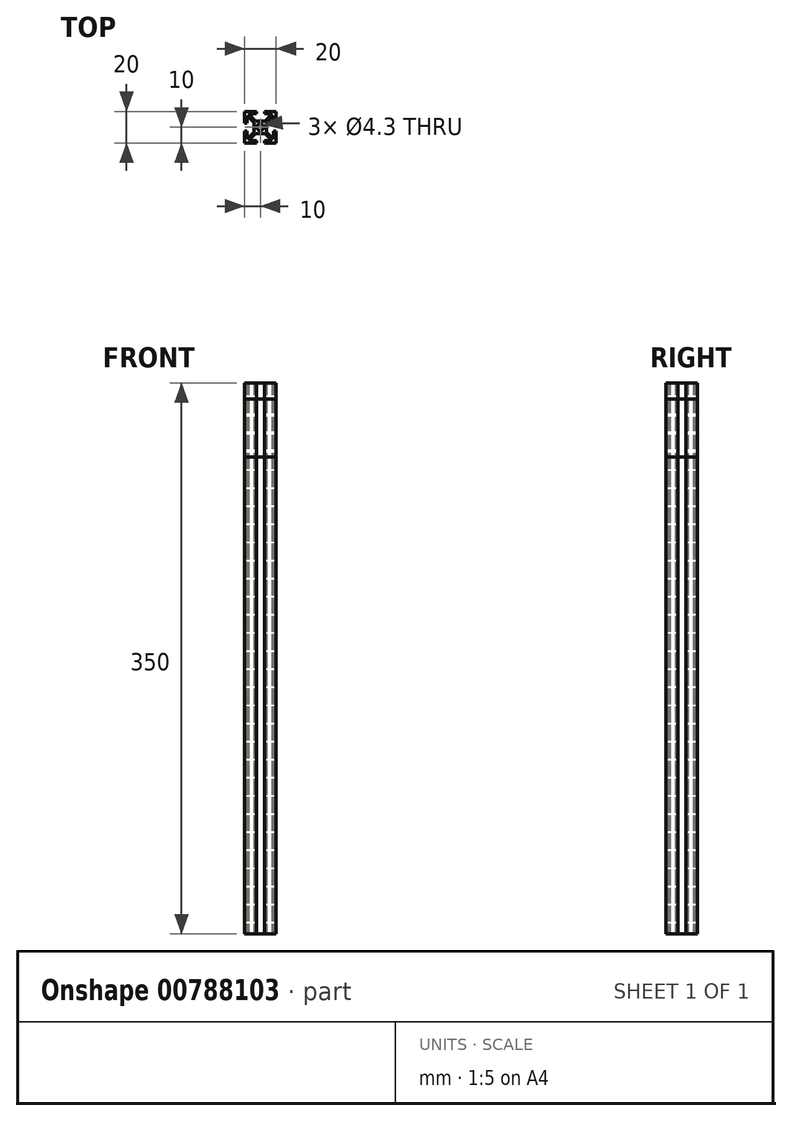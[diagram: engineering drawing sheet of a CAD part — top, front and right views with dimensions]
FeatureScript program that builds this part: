
annotation { "Feature Type Name" : "Feature", "Feature Type Description" : "" }
export const myFeature = defineFeature(function(context is Context, id is Id, definition is map)
    precondition{}
    {
        {
            var Q0;
            Q0=qCreatedBy(makeId("Top.planeOp"),FACE);
            var sketch = newSketch(context, id + "F0", { "sketchPlane" : qUnion([Q0])});
            skCircle(sketch, "E0", {"center": v(0, 0) * mm, "radius": 2.15 * mm});
            skLineSegment(sketch, "E1.bottom", {"start": v(10, 10) * mm, "end": v(-10, 10) * mm});
            skLineSegment(sketch, "E1.top", {"start": v(10, -10) * mm, "end": v(-10, -10) * mm});
            skLineSegment(sketch, "E1.left", {"start": v(10, 10) * mm, "end": v(10, -10) * mm});
            skLineSegment(sketch, "E1.right", {"start": v(-10, 10) * mm, "end": v(-10, -10) * mm});
            skLineSegment(sketch, "E2.bottom", {"start": v(8.5, 8.5) * mm, "end": v(-8.5, 8.5) * mm});
            skLineSegment(sketch, "E2.top", {"start": v(8.5, -8.5) * mm, "end": v(-8.5, -8.5) * mm});
            skLineSegment(sketch, "E2.left", {"start": v(8.5, 8.5) * mm, "end": v(8.5, -8.5) * mm});
            skLineSegment(sketch, "E2.right", {"start": v(-8.5, 8.5) * mm, "end": v(-8.5, -8.5) * mm});
            skLineSegment(sketch, "E3.bottom", {"start": v(4, 4) * mm, "end": v(-4, 4) * mm});
            skLineSegment(sketch, "E3.top", {"start": v(4, -4) * mm, "end": v(-4, -4) * mm});
            skLineSegment(sketch, "E3.left", {"start": v(4, 4) * mm, "end": v(4, -4) * mm});
            skLineSegment(sketch, "E3.right", {"start": v(-4, 4) * mm, "end": v(-4, -4) * mm});
            skLineSegment(sketch, "E4", {"start": v(8.5, 8.5) * mm, "end": v(-8.5, -8.5) * mm, "construction": true});
            skLineSegment(sketch, "E5", {"start": v(-8.5, 8.5) * mm, "end": v(8.5, -8.5) * mm, "construction": true});
            skLineSegment(sketch, "E6.0", {"start": v(-9.03, 7.97) * mm, "end": v(7.97, -9.03) * mm});
            skLineSegment(sketch, "E7.0", {"start": v(-7.97, 9.03) * mm, "end": v(9.03, -7.97) * mm});
            skLineSegment(sketch, "E8.0", {"start": v(7.97, 9.03) * mm, "end": v(-9.03, -7.97) * mm});
            skLineSegment(sketch, "E9.0", {"start": v(9.03, 7.97) * mm, "end": v(-7.97, -9.03) * mm});
            skLineSegment(sketch, "E10", {"start": v(0, 10) * mm, "end": v(0, -10) * mm, "construction": true});
            skLineSegment(sketch, "E11", {"start": v(-10, 0) * mm, "end": v(10, 0) * mm, "construction": true});
            skLineSegment(sketch, "E12.0", {"start": v(-10, -2.5) * mm, "end": v(10, -2.5) * mm});
            skLineSegment(sketch, "E13.0", {"start": v(-10, 2.5) * mm, "end": v(10, 2.5) * mm});
            skLineSegment(sketch, "E14.0", {"start": v(-2.5, 10) * mm, "end": v(-2.5, -10) * mm});
            skLineSegment(sketch, "E15.0", {"start": v(2.5, 10) * mm, "end": v(2.5, -10) * mm});
            skSolve(sketch);
        }
        {
            var Q0;
            {var subQ7=sQuery(id+"F0.wireOp",EDGE,"E1.right");var subQ8=sQuery(id+"F0.wireOp",EDGE,"E1.bottom");var subQ9=makeQuery(id+"F0.imprint","INTERSECT",VERTEX,{"derivedFrom":[subQ8,subQ7]});Q0=makeQuery(id+"F0.imprint","IMPRINT",FACE,{"disambiguationData":[TD([[makeQuery(id+"F0.imprint","IMPRINT",EDGE,{"disambiguationData":[TD([[subQ9,1.0]])],"derivedFrom":subQ8}),1.0]])]});}
            var Q1;
            {var subQ7=sQuery(id+"F0.wireOp",EDGE,"E2.right");var subQ8=sQuery(id+"F0.wireOp",EDGE,"E2.bottom");var subQ9=makeQuery(id+"F0.imprint","INTERSECT",VERTEX,{"derivedFrom":[subQ8,subQ7]});Q1=makeQuery(id+"F0.imprint","IMPRINT",FACE,{"disambiguationData":[TD([[makeQuery(id+"F0.imprint","IMPRINT",EDGE,{"disambiguationData":[TD([[subQ9,1.0]])],"derivedFrom":subQ8}),1.0]])]});}
            var Q2;
            {var subQ1=sQuery(id+"F0.wireOp",EDGE,"E3.right");var subQ5=sQuery(id+"F0.wireOp",EDGE,"E13.0");var subQ10=makeQuery(id+"F0.imprint","INTERSECT",VERTEX,{"derivedFrom":[subQ1,subQ5]});Q2=makeQuery(id+"F0.imprint","IMPRINT",FACE,{"disambiguationData":[TD([[makeQuery(id+"F0.imprint","IMPRINT",EDGE,{"disambiguationData":[TD([[subQ10,-1.0]])],"derivedFrom":subQ1}),1.0]])]});}
            var Q3;
            {var subQ1=sQuery(id+"F0.wireOp",EDGE,"E3.bottom");var subQ6=sQuery(id+"F0.wireOp",EDGE,"E3.right");var subQ10=makeQuery(id+"F0.imprint","INTERSECT",VERTEX,{"derivedFrom":[subQ1,subQ6]});Q3=makeQuery(id+"F0.imprint","IMPRINT",FACE,{"disambiguationData":[TD([[makeQuery(id+"F0.imprint","IMPRINT",EDGE,{"disambiguationData":[TD([[subQ10,1.0]])],"derivedFrom":subQ1}),1.0]])]});}
            var Q4;
            {var subQ0=sQuery(id+"F0.wireOp",EDGE,"E6.0");var subQ1=sQuery(id+"F0.wireOp",EDGE,"E3.right");var subQ2=makeQuery(id+"F0.imprint","INTERSECT",VERTEX,{"derivedFrom":[subQ1,subQ0]});Q4=makeQuery(id+"F0.imprint","IMPRINT",FACE,{"disambiguationData":[TD([[makeQuery(id+"F0.imprint","IMPRINT",EDGE,{"disambiguationData":[TD([[subQ2,-1.0]])],"derivedFrom":subQ1}),1.0]])]});}
            var Q5;
            {var subQ0=sQuery(id+"F0.wireOp",EDGE,"E12.0");var subQ1=sQuery(id+"F0.wireOp",EDGE,"E3.right");var subQ2=makeQuery(id+"F0.imprint","INTERSECT",VERTEX,{"derivedFrom":[subQ1,subQ0]});Q5=makeQuery(id+"F0.imprint","IMPRINT",FACE,{"disambiguationData":[TD([[makeQuery(id+"F0.imprint","IMPRINT",EDGE,{"disambiguationData":[TD([[subQ2,-1.0]])],"derivedFrom":subQ1}),1.0]])]});}
            var Q6;
            {var subQ1=sQuery(id+"F0.wireOp",EDGE,"E3.top");var subQ6=sQuery(id+"F0.wireOp",EDGE,"E3.right");var subQ10=makeQuery(id+"F0.imprint","INTERSECT",VERTEX,{"derivedFrom":[subQ1,subQ6]});Q6=makeQuery(id+"F0.imprint","IMPRINT",FACE,{"disambiguationData":[TD([[makeQuery(id+"F0.imprint","IMPRINT",EDGE,{"disambiguationData":[TD([[subQ10,1.0]])],"derivedFrom":subQ1}),-1.0]])]});}
            var Q7;
            {var subQ5=sQuery(id+"F0.wireOp",EDGE,"E2.right");var subQ8=sQuery(id+"F0.wireOp",EDGE,"E2.top");var subQ11=makeQuery(id+"F0.imprint","INTERSECT",VERTEX,{"derivedFrom":[subQ8,subQ5]});Q7=makeQuery(id+"F0.imprint","IMPRINT",FACE,{"disambiguationData":[TD([[makeQuery(id+"F0.imprint","IMPRINT",EDGE,{"disambiguationData":[TD([[subQ11,1.0]])],"derivedFrom":subQ8}),-1.0]])]});}
            var Q8;
            {var subQ0=sQuery(id+"F0.wireOp",EDGE,"E14.0");var subQ1=sQuery(id+"F0.wireOp",EDGE,"E8.0");var subQ2=makeQuery(id+"F0.imprint","INTERSECT",VERTEX,{"derivedFrom":[subQ1,subQ0]});Q8=makeQuery(id+"F0.imprint","IMPRINT",FACE,{"disambiguationData":[TD([[makeQuery(id+"F0.imprint","IMPRINT",EDGE,{"disambiguationData":[TD([[subQ2,-1.0]])],"derivedFrom":subQ1}),1.0]])]});}
            var Q9;
            {var subQ0=sQuery(id+"F0.wireOp",EDGE,"E13.0");var subQ1=sQuery(id+"F0.wireOp",EDGE,"E6.0");var subQ2=makeQuery(id+"F0.imprint","INTERSECT",VERTEX,{"derivedFrom":[subQ1,subQ0]});Q9=makeQuery(id+"F0.imprint","IMPRINT",FACE,{"disambiguationData":[TD([[makeQuery(id+"F0.imprint","IMPRINT",EDGE,{"disambiguationData":[TD([[subQ2,-1.0]])],"derivedFrom":subQ1}),1.0]])]});}
            var Q10;
            {var subQ0=sQuery(id+"F0.wireOp",EDGE,"E14.0");var subQ1=sQuery(id+"F0.wireOp",EDGE,"E3.bottom");var subQ2=makeQuery(id+"F0.imprint","INTERSECT",VERTEX,{"derivedFrom":[subQ1,subQ0]});Q10=makeQuery(id+"F0.imprint","IMPRINT",FACE,{"disambiguationData":[TD([[makeQuery(id+"F0.imprint","IMPRINT",EDGE,{"disambiguationData":[TD([[subQ2,-1.0]])],"derivedFrom":subQ1}),1.0]])]});}
            var Q11;
            {var subQ5=sQuery(id+"F0.wireOp",EDGE,"E15.0");var subQ9=sQuery(id+"F0.wireOp",EDGE,"E3.bottom");var subQ11=makeQuery(id+"F0.imprint","INTERSECT",VERTEX,{"derivedFrom":[subQ9,subQ5]});Q11=makeQuery(id+"F0.imprint","IMPRINT",FACE,{"disambiguationData":[TD([[makeQuery(id+"F0.imprint","IMPRINT",EDGE,{"disambiguationData":[TD([[subQ11,-1.0]])],"derivedFrom":subQ9}),1.0]])]});}
            var Q12;
            {var subQ0=sQuery(id+"F0.wireOp",EDGE,"E14.0");var subQ1=sQuery(id+"F0.wireOp",EDGE,"E7.0");var subQ2=makeQuery(id+"F0.imprint","INTERSECT",VERTEX,{"derivedFrom":[subQ1,subQ0]});Q12=makeQuery(id+"F0.imprint","IMPRINT",FACE,{"disambiguationData":[TD([[makeQuery(id+"F0.imprint","IMPRINT",EDGE,{"disambiguationData":[TD([[subQ2,-1.0]])],"derivedFrom":subQ1}),-1.0]])]});}
            var Q13;
            {var subQ0=sQuery(id+"F0.wireOp",EDGE,"E15.0");var subQ1=sQuery(id+"F0.wireOp",EDGE,"E8.0");var subQ2=makeQuery(id+"F0.imprint","INTERSECT",VERTEX,{"derivedFrom":[subQ1,subQ0]});Q13=makeQuery(id+"F0.imprint","IMPRINT",FACE,{"disambiguationData":[TD([[makeQuery(id+"F0.imprint","IMPRINT",EDGE,{"disambiguationData":[TD([[subQ2,-1.0]])],"derivedFrom":subQ1}),1.0]])]});}
            var Q14;
            {var subQ1=sQuery(id+"F0.wireOp",EDGE,"E3.left");var subQ6=sQuery(id+"F0.wireOp",EDGE,"E3.bottom");var subQ10=makeQuery(id+"F0.imprint","INTERSECT",VERTEX,{"derivedFrom":[subQ6,subQ1]});Q14=makeQuery(id+"F0.imprint","IMPRINT",FACE,{"disambiguationData":[TD([[makeQuery(id+"F0.imprint","IMPRINT",EDGE,{"disambiguationData":[TD([[subQ10,-1.0]])],"derivedFrom":subQ6}),1.0]])]});}
            var Q15;
            {var subQ0=sQuery(id+"F0.wireOp",EDGE,"E8.0");var subQ1=sQuery(id+"F0.wireOp",EDGE,"E3.bottom");var subQ2=makeQuery(id+"F0.imprint","INTERSECT",VERTEX,{"derivedFrom":[subQ1,subQ0]});Q15=makeQuery(id+"F0.imprint","IMPRINT",FACE,{"disambiguationData":[TD([[makeQuery(id+"F0.imprint","IMPRINT",EDGE,{"disambiguationData":[TD([[subQ2,-1.0]])],"derivedFrom":subQ1}),1.0]])]});}
            var Q16;
            {var subQ0=sQuery(id+"F0.wireOp",EDGE,"E9.0");var subQ1=sQuery(id+"F0.wireOp",EDGE,"E3.left");var subQ2=makeQuery(id+"F0.imprint","INTERSECT",VERTEX,{"derivedFrom":[subQ1,subQ0]});Q16=makeQuery(id+"F0.imprint","IMPRINT",FACE,{"disambiguationData":[TD([[makeQuery(id+"F0.imprint","IMPRINT",EDGE,{"disambiguationData":[TD([[subQ2,-1.0]])],"derivedFrom":subQ1}),-1.0]])]});}
            var Q17;
            {var subQ0=sQuery(id+"F0.wireOp",EDGE,"E13.0");var subQ9=sQuery(id+"F0.wireOp",EDGE,"E3.left");var subQ11=makeQuery(id+"F0.imprint","INTERSECT",VERTEX,{"derivedFrom":[subQ9,subQ0]});Q17=makeQuery(id+"F0.imprint","IMPRINT",FACE,{"disambiguationData":[TD([[makeQuery(id+"F0.imprint","IMPRINT",EDGE,{"disambiguationData":[TD([[subQ11,-1.0]])],"derivedFrom":subQ9}),-1.0]])]});}
            var Q18;
            {var subQ1=sQuery(id+"F0.wireOp",EDGE,"E3.top");var subQ6=sQuery(id+"F0.wireOp",EDGE,"E3.left");var subQ10=makeQuery(id+"F0.imprint","INTERSECT",VERTEX,{"derivedFrom":[subQ1,subQ6]});Q18=makeQuery(id+"F0.imprint","IMPRINT",FACE,{"disambiguationData":[TD([[makeQuery(id+"F0.imprint","IMPRINT",EDGE,{"disambiguationData":[TD([[subQ10,-1.0]])],"derivedFrom":subQ1}),-1.0]])]});}
            var Q19;
            {var subQ0=sQuery(id+"F0.wireOp",EDGE,"E15.0");var subQ1=sQuery(id+"F0.wireOp",EDGE,"E7.0");var subQ2=makeQuery(id+"F0.imprint","INTERSECT",VERTEX,{"derivedFrom":[subQ1,subQ0]});Q19=makeQuery(id+"F0.imprint","IMPRINT",FACE,{"disambiguationData":[TD([[makeQuery(id+"F0.imprint","IMPRINT",EDGE,{"disambiguationData":[TD([[subQ2,-1.0]])],"derivedFrom":subQ1}),-1.0]])]});}
            var Q20;
            {var subQ0=sQuery(id+"F0.wireOp",EDGE,"E12.0");var subQ1=sQuery(id+"F0.wireOp",EDGE,"E6.0");var subQ2=makeQuery(id+"F0.imprint","INTERSECT",VERTEX,{"derivedFrom":[subQ1,subQ0]});Q20=makeQuery(id+"F0.imprint","IMPRINT",FACE,{"disambiguationData":[TD([[makeQuery(id+"F0.imprint","IMPRINT",EDGE,{"disambiguationData":[TD([[subQ2,-1.0]])],"derivedFrom":subQ1}),1.0]])]});}
            var Q21;
            {var subQ7=sQuery(id+"F0.wireOp",EDGE,"E15.0");var subQ9=sQuery(id+"F0.wireOp",EDGE,"E3.top");var subQ11=makeQuery(id+"F0.imprint","INTERSECT",VERTEX,{"derivedFrom":[subQ9,subQ7]});Q21=makeQuery(id+"F0.imprint","IMPRINT",FACE,{"disambiguationData":[TD([[makeQuery(id+"F0.imprint","IMPRINT",EDGE,{"disambiguationData":[TD([[subQ11,-1.0]])],"derivedFrom":subQ9}),-1.0]])]});}
            var Q22;
            {var subQ0=sQuery(id+"F0.wireOp",EDGE,"E14.0");var subQ1=sQuery(id+"F0.wireOp",EDGE,"E3.top");var subQ2=makeQuery(id+"F0.imprint","INTERSECT",VERTEX,{"derivedFrom":[subQ1,subQ0]});Q22=makeQuery(id+"F0.imprint","IMPRINT",FACE,{"disambiguationData":[TD([[makeQuery(id+"F0.imprint","IMPRINT",EDGE,{"disambiguationData":[TD([[subQ2,-1.0]])],"derivedFrom":subQ1}),-1.0]])]});}
            var Q23;
            {var subQ0=sQuery(id+"F0.wireOp",EDGE,"E12.0");var subQ1=sQuery(id+"F0.wireOp",EDGE,"E3.left");var subQ2=makeQuery(id+"F0.imprint","INTERSECT",VERTEX,{"derivedFrom":[subQ1,subQ0]});Q23=makeQuery(id+"F0.imprint","IMPRINT",FACE,{"disambiguationData":[TD([[makeQuery(id+"F0.imprint","IMPRINT",EDGE,{"disambiguationData":[TD([[subQ2,-1.0]])],"derivedFrom":subQ1}),-1.0]])]});}
            var Q24;
            {var subQ0=sQuery(id+"F0.wireOp",EDGE,"E6.0");var subQ1=sQuery(id+"F0.wireOp",EDGE,"E3.top");var subQ2=makeQuery(id+"F0.imprint","INTERSECT",VERTEX,{"derivedFrom":[subQ1,subQ0]});Q24=makeQuery(id+"F0.imprint","IMPRINT",FACE,{"disambiguationData":[TD([[makeQuery(id+"F0.imprint","IMPRINT",EDGE,{"disambiguationData":[TD([[subQ2,-1.0]])],"derivedFrom":subQ1}),-1.0]])]});}
            var Q25;
            {var subQ5=sQuery(id+"F0.wireOp",EDGE,"E2.left");var subQ6=sQuery(id+"F0.wireOp",EDGE,"E2.top");var subQ7=makeQuery(id+"F0.imprint","INTERSECT",VERTEX,{"derivedFrom":[subQ6,subQ5]});Q25=makeQuery(id+"F0.imprint","IMPRINT",FACE,{"disambiguationData":[TD([[makeQuery(id+"F0.imprint","IMPRINT",EDGE,{"disambiguationData":[TD([[subQ7,-1.0]])],"derivedFrom":subQ6}),-1.0]])]});}
            var Q26;
            {var subQ0=sQuery(id+"F0.wireOp",EDGE,"E12.0");var subQ1=sQuery(id+"F0.wireOp",EDGE,"E9.0");var subQ2=makeQuery(id+"F0.imprint","INTERSECT",VERTEX,{"derivedFrom":[subQ1,subQ0]});Q26=makeQuery(id+"F0.imprint","IMPRINT",FACE,{"disambiguationData":[TD([[makeQuery(id+"F0.imprint","IMPRINT",EDGE,{"disambiguationData":[TD([[subQ2,-1.0]])],"derivedFrom":subQ1}),-1.0]])]});}
            var Q27;
            {var subQ0=sQuery(id+"F0.wireOp",EDGE,"E13.0");var subQ1=sQuery(id+"F0.wireOp",EDGE,"E9.0");var subQ2=makeQuery(id+"F0.imprint","INTERSECT",VERTEX,{"derivedFrom":[subQ1,subQ0]});Q27=makeQuery(id+"F0.imprint","IMPRINT",FACE,{"disambiguationData":[TD([[makeQuery(id+"F0.imprint","IMPRINT",EDGE,{"disambiguationData":[TD([[subQ2,-1.0]])],"derivedFrom":subQ1}),-1.0]])]});}
            var Q28;
            {var subQ7=sQuery(id+"F0.wireOp",EDGE,"E2.left");var subQ8=sQuery(id+"F0.wireOp",EDGE,"E2.bottom");var subQ9=makeQuery(id+"F0.imprint","INTERSECT",VERTEX,{"derivedFrom":[subQ8,subQ7]});Q28=makeQuery(id+"F0.imprint","IMPRINT",FACE,{"disambiguationData":[TD([[makeQuery(id+"F0.imprint","IMPRINT",EDGE,{"disambiguationData":[TD([[subQ9,-1.0]])],"derivedFrom":subQ8}),1.0]])]});}
            var Q29;
            {var subQ9=sQuery(id+"F0.wireOp",EDGE,"E1.left");var subQ10=sQuery(id+"F0.wireOp",EDGE,"E1.bottom");var subQ11=makeQuery(id+"F0.imprint","INTERSECT",VERTEX,{"derivedFrom":[subQ10,subQ9]});Q29=makeQuery(id+"F0.imprint","IMPRINT",FACE,{"disambiguationData":[TD([[makeQuery(id+"F0.imprint","IMPRINT",EDGE,{"disambiguationData":[TD([[subQ11,-1.0]])],"derivedFrom":subQ10}),1.0]])]});}
            var Q30;
            {var subQ7=sQuery(id+"F0.wireOp",EDGE,"E1.left");var subQ10=sQuery(id+"F0.wireOp",EDGE,"E1.top");var subQ12=makeQuery(id+"F0.imprint","INTERSECT",VERTEX,{"derivedFrom":[subQ10,subQ7]});Q30=makeQuery(id+"F0.imprint","IMPRINT",FACE,{"disambiguationData":[TD([[makeQuery(id+"F0.imprint","IMPRINT",EDGE,{"disambiguationData":[TD([[subQ12,-1.0]])],"derivedFrom":subQ10}),-1.0]])]});}
            var Q31;
            {var subQ4=sQuery(id+"F0.wireOp",EDGE,"E1.right");var subQ5=sQuery(id+"F0.wireOp",EDGE,"E1.top");var subQ6=makeQuery(id+"F0.imprint","INTERSECT",VERTEX,{"derivedFrom":[subQ5,subQ4]});Q31=makeQuery(id+"F0.imprint","IMPRINT",FACE,{"disambiguationData":[TD([[makeQuery(id+"F0.imprint","IMPRINT",EDGE,{"disambiguationData":[TD([[subQ6,1.0]])],"derivedFrom":subQ5}),-1.0]])]});}
            var Q32;
            {var subQ1=sQuery(id+"F0.wireOp",EDGE,"E7.0");var subQ7=sQuery(id+"F0.wireOp",EDGE,"E0");var subQ8=makeQuery(id+"F0.imprint","INTERSECT",VERTEX,{"disambiguationData":[OD(0.0)],"derivedFrom":[subQ7,subQ1]});Q32=makeQuery(id+"F0.imprint","IMPRINT",FACE,{"disambiguationData":[TD([[makeQuery(id+"F0.imprint","IMPRINT",EDGE,{"disambiguationData":[TD([[subQ8,-1.0]])],"derivedFrom":subQ7}),-1.0]])]});}
            var Q33;
            {var subQ0=sQuery(id+"F0.wireOp",EDGE,"E8.0");var subQ1=sQuery(id+"F0.wireOp",EDGE,"E0");var subQ2=makeQuery(id+"F0.imprint","INTERSECT",VERTEX,{"disambiguationData":[OD(0.0)],"derivedFrom":[subQ1,subQ0]});Q33=makeQuery(id+"F0.imprint","IMPRINT",FACE,{"disambiguationData":[TD([[makeQuery(id+"F0.imprint","IMPRINT",EDGE,{"disambiguationData":[TD([[subQ2,-1.0]])],"derivedFrom":subQ1}),-1.0]])]});}
            var Q34;
            {var subQ1=sQuery(id+"F0.wireOp",EDGE,"E8.0");var subQ5=sQuery(id+"F0.wireOp",EDGE,"E0");var subQ6=makeQuery(id+"F0.imprint","INTERSECT",VERTEX,{"disambiguationData":[OD(0.0)],"derivedFrom":[subQ5,subQ1]});Q34=makeQuery(id+"F0.imprint","IMPRINT",FACE,{"disambiguationData":[TD([[makeQuery(id+"F0.imprint","IMPRINT",EDGE,{"disambiguationData":[TD([[subQ6,1.0]])],"derivedFrom":subQ5}),-1.0]])]});}
            var Q35;
            {var subQ0=sQuery(id+"F0.wireOp",EDGE,"E9.0");var subQ1=sQuery(id+"F0.wireOp",EDGE,"E0");var subQ2=makeQuery(id+"F0.imprint","INTERSECT",VERTEX,{"disambiguationData":[OD(0.0)],"derivedFrom":[subQ1,subQ0]});Q35=makeQuery(id+"F0.imprint","IMPRINT",FACE,{"disambiguationData":[TD([[makeQuery(id+"F0.imprint","IMPRINT",EDGE,{"disambiguationData":[TD([[subQ2,1.0]])],"derivedFrom":subQ1}),-1.0]])]});}
            var Q36;
            {var subQ1=sQuery(id+"F0.wireOp",EDGE,"E6.0");var subQ7=sQuery(id+"F0.wireOp",EDGE,"E0");var subQ9=makeQuery(id+"F0.imprint","INTERSECT",VERTEX,{"disambiguationData":[OD(1.0)],"derivedFrom":[subQ7,subQ1]});Q36=makeQuery(id+"F0.imprint","IMPRINT",FACE,{"disambiguationData":[TD([[makeQuery(id+"F0.imprint","IMPRINT",EDGE,{"disambiguationData":[TD([[subQ9,-1.0]])],"derivedFrom":subQ7}),-1.0]])]});}
            var Q37;
            {var subQ0=sQuery(id+"F0.wireOp",EDGE,"E9.0");var subQ1=sQuery(id+"F0.wireOp",EDGE,"E0");var subQ2=makeQuery(id+"F0.imprint","INTERSECT",VERTEX,{"disambiguationData":[OD(1.0)],"derivedFrom":[subQ1,subQ0]});Q37=makeQuery(id+"F0.imprint","IMPRINT",FACE,{"disambiguationData":[TD([[makeQuery(id+"F0.imprint","IMPRINT",EDGE,{"disambiguationData":[TD([[subQ2,-1.0]])],"derivedFrom":subQ1}),-1.0]])]});}
            var Q38;
            {var subQ5=sQuery(id+"F0.wireOp",EDGE,"E0");var subQ7=sQuery(id+"F0.wireOp",EDGE,"E8.0");var subQ8=makeQuery(id+"F0.imprint","INTERSECT",VERTEX,{"disambiguationData":[OD(1.0)],"derivedFrom":[subQ5,subQ7]});Q38=makeQuery(id+"F0.imprint","IMPRINT",FACE,{"disambiguationData":[TD([[makeQuery(id+"F0.imprint","IMPRINT",EDGE,{"disambiguationData":[TD([[subQ8,-1.0]])],"derivedFrom":subQ5}),-1.0]])]});}
            var Q39;
            {var subQ0=sQuery(id+"F0.wireOp",EDGE,"E6.0");var subQ1=sQuery(id+"F0.wireOp",EDGE,"E0");var subQ2=makeQuery(id+"F0.imprint","INTERSECT",VERTEX,{"disambiguationData":[OD(0.0)],"derivedFrom":[subQ1,subQ0]});Q39=makeQuery(id+"F0.imprint","IMPRINT",FACE,{"disambiguationData":[TD([[makeQuery(id+"F0.imprint","IMPRINT",EDGE,{"disambiguationData":[TD([[subQ2,-1.0]])],"derivedFrom":subQ1}),-1.0]])]});}
            extrude(context, id + "F1", {"entities" : qUnion([Q0, Q1, Q2, Q3, Q4, Q5, Q6, Q7, Q8, Q9, Q10, Q11, Q12, Q13, Q14, Q15, Q16, Q17, Q18, Q19, Q20, Q21, Q22, Q23, Q24, Q25, Q26, Q27, Q28, Q29, Q30, Q31, Q32, Q33, Q34, Q35, Q36, Q37, Q38, Q39]), "depth" : 340 * mm, "offsetDistance" : 25 * mm});
        }
        {
            var Q0;
            {var subQ0=sQuery(id+"F0.wireOp",EDGE,"E12.0");var subQ1=sQuery(id+"F0.wireOp",EDGE,"E6.0");var subQ2=makeQuery(id+"F0.imprint","INTERSECT",VERTEX,{"derivedFrom":[subQ1,subQ0]});Q0=makeQuery(id+"F0.imprint","IMPRINT",FACE,{"disambiguationData":[TD([[makeQuery(id+"F0.imprint","IMPRINT",EDGE,{"disambiguationData":[TD([[subQ2,-1.0]])],"derivedFrom":subQ1}),1.0]])]});}
            var Q1;
            {var subQ5=sQuery(id+"F0.wireOp",EDGE,"E0");var subQ7=sQuery(id+"F0.wireOp",EDGE,"E8.0");var subQ8=makeQuery(id+"F0.imprint","INTERSECT",VERTEX,{"disambiguationData":[OD(1.0)],"derivedFrom":[subQ5,subQ7]});Q1=makeQuery(id+"F0.imprint","IMPRINT",FACE,{"disambiguationData":[TD([[makeQuery(id+"F0.imprint","IMPRINT",EDGE,{"disambiguationData":[TD([[subQ8,-1.0]])],"derivedFrom":subQ5}),-1.0]])]});}
            var Q2;
            {var subQ0=sQuery(id+"F0.wireOp",EDGE,"E12.0");var subQ1=sQuery(id+"F0.wireOp",EDGE,"E9.0");var subQ2=makeQuery(id+"F0.imprint","INTERSECT",VERTEX,{"derivedFrom":[subQ1,subQ0]});Q2=makeQuery(id+"F0.imprint","IMPRINT",FACE,{"disambiguationData":[TD([[makeQuery(id+"F0.imprint","IMPRINT",EDGE,{"disambiguationData":[TD([[subQ2,-1.0]])],"derivedFrom":subQ1}),-1.0]])]});}
            var Q3;
            {var subQ0=sQuery(id+"F0.wireOp",EDGE,"E13.0");var subQ1=sQuery(id+"F0.wireOp",EDGE,"E9.0");var subQ2=makeQuery(id+"F0.imprint","INTERSECT",VERTEX,{"derivedFrom":[subQ1,subQ0]});Q3=makeQuery(id+"F0.imprint","IMPRINT",FACE,{"disambiguationData":[TD([[makeQuery(id+"F0.imprint","IMPRINT",EDGE,{"disambiguationData":[TD([[subQ2,-1.0]])],"derivedFrom":subQ1}),-1.0]])]});}
            var Q4;
            {var subQ1=sQuery(id+"F0.wireOp",EDGE,"E3.right");var subQ5=sQuery(id+"F0.wireOp",EDGE,"E13.0");var subQ10=makeQuery(id+"F0.imprint","INTERSECT",VERTEX,{"derivedFrom":[subQ1,subQ5]});Q4=makeQuery(id+"F0.imprint","IMPRINT",FACE,{"disambiguationData":[TD([[makeQuery(id+"F0.imprint","IMPRINT",EDGE,{"disambiguationData":[TD([[subQ10,-1.0]])],"derivedFrom":subQ1}),1.0]])]});}
            var Q5;
            {var subQ0=sQuery(id+"F0.wireOp",EDGE,"E13.0");var subQ9=sQuery(id+"F0.wireOp",EDGE,"E3.left");var subQ11=makeQuery(id+"F0.imprint","INTERSECT",VERTEX,{"derivedFrom":[subQ9,subQ0]});Q5=makeQuery(id+"F0.imprint","IMPRINT",FACE,{"disambiguationData":[TD([[makeQuery(id+"F0.imprint","IMPRINT",EDGE,{"disambiguationData":[TD([[subQ11,-1.0]])],"derivedFrom":subQ9}),-1.0]])]});}
            var Q6;
            {var subQ1=sQuery(id+"F0.wireOp",EDGE,"E3.bottom");var subQ6=sQuery(id+"F0.wireOp",EDGE,"E3.right");var subQ10=makeQuery(id+"F0.imprint","INTERSECT",VERTEX,{"derivedFrom":[subQ1,subQ6]});Q6=makeQuery(id+"F0.imprint","IMPRINT",FACE,{"disambiguationData":[TD([[makeQuery(id+"F0.imprint","IMPRINT",EDGE,{"disambiguationData":[TD([[subQ10,1.0]])],"derivedFrom":subQ1}),1.0]])]});}
            var Q7;
            {var subQ0=sQuery(id+"F0.wireOp",EDGE,"E13.0");var subQ1=sQuery(id+"F0.wireOp",EDGE,"E6.0");var subQ2=makeQuery(id+"F0.imprint","INTERSECT",VERTEX,{"derivedFrom":[subQ1,subQ0]});Q7=makeQuery(id+"F0.imprint","IMPRINT",FACE,{"disambiguationData":[TD([[makeQuery(id+"F0.imprint","IMPRINT",EDGE,{"disambiguationData":[TD([[subQ2,-1.0]])],"derivedFrom":subQ1}),1.0]])]});}
            var Q8;
            {var subQ5=sQuery(id+"F0.wireOp",EDGE,"E2.right");var subQ8=sQuery(id+"F0.wireOp",EDGE,"E2.top");var subQ11=makeQuery(id+"F0.imprint","INTERSECT",VERTEX,{"derivedFrom":[subQ8,subQ5]});Q8=makeQuery(id+"F0.imprint","IMPRINT",FACE,{"disambiguationData":[TD([[makeQuery(id+"F0.imprint","IMPRINT",EDGE,{"disambiguationData":[TD([[subQ11,1.0]])],"derivedFrom":subQ8}),-1.0]])]});}
            var Q9;
            {var subQ5=sQuery(id+"F0.wireOp",EDGE,"E15.0");var subQ9=sQuery(id+"F0.wireOp",EDGE,"E3.bottom");var subQ11=makeQuery(id+"F0.imprint","INTERSECT",VERTEX,{"derivedFrom":[subQ9,subQ5]});Q9=makeQuery(id+"F0.imprint","IMPRINT",FACE,{"disambiguationData":[TD([[makeQuery(id+"F0.imprint","IMPRINT",EDGE,{"disambiguationData":[TD([[subQ11,-1.0]])],"derivedFrom":subQ9}),1.0]])]});}
            var Q10;
            {var subQ7=sQuery(id+"F0.wireOp",EDGE,"E1.right");var subQ8=sQuery(id+"F0.wireOp",EDGE,"E1.bottom");var subQ9=makeQuery(id+"F0.imprint","INTERSECT",VERTEX,{"derivedFrom":[subQ8,subQ7]});Q10=makeQuery(id+"F0.imprint","IMPRINT",FACE,{"disambiguationData":[TD([[makeQuery(id+"F0.imprint","IMPRINT",EDGE,{"disambiguationData":[TD([[subQ9,1.0]])],"derivedFrom":subQ8}),1.0]])]});}
            var Q11;
            {var subQ1=sQuery(id+"F0.wireOp",EDGE,"E3.top");var subQ6=sQuery(id+"F0.wireOp",EDGE,"E3.right");var subQ10=makeQuery(id+"F0.imprint","INTERSECT",VERTEX,{"derivedFrom":[subQ1,subQ6]});Q11=makeQuery(id+"F0.imprint","IMPRINT",FACE,{"disambiguationData":[TD([[makeQuery(id+"F0.imprint","IMPRINT",EDGE,{"disambiguationData":[TD([[subQ10,1.0]])],"derivedFrom":subQ1}),-1.0]])]});}
            var Q12;
            {var subQ7=sQuery(id+"F0.wireOp",EDGE,"E2.left");var subQ8=sQuery(id+"F0.wireOp",EDGE,"E2.bottom");var subQ9=makeQuery(id+"F0.imprint","INTERSECT",VERTEX,{"derivedFrom":[subQ8,subQ7]});Q12=makeQuery(id+"F0.imprint","IMPRINT",FACE,{"disambiguationData":[TD([[makeQuery(id+"F0.imprint","IMPRINT",EDGE,{"disambiguationData":[TD([[subQ9,-1.0]])],"derivedFrom":subQ8}),1.0]])]});}
            var Q13;
            {var subQ5=sQuery(id+"F0.wireOp",EDGE,"E2.left");var subQ6=sQuery(id+"F0.wireOp",EDGE,"E2.top");var subQ7=makeQuery(id+"F0.imprint","INTERSECT",VERTEX,{"derivedFrom":[subQ6,subQ5]});Q13=makeQuery(id+"F0.imprint","IMPRINT",FACE,{"disambiguationData":[TD([[makeQuery(id+"F0.imprint","IMPRINT",EDGE,{"disambiguationData":[TD([[subQ7,-1.0]])],"derivedFrom":subQ6}),-1.0]])]});}
            var Q14;
            {var subQ9=sQuery(id+"F0.wireOp",EDGE,"E1.left");var subQ10=sQuery(id+"F0.wireOp",EDGE,"E1.bottom");var subQ11=makeQuery(id+"F0.imprint","INTERSECT",VERTEX,{"derivedFrom":[subQ10,subQ9]});Q14=makeQuery(id+"F0.imprint","IMPRINT",FACE,{"disambiguationData":[TD([[makeQuery(id+"F0.imprint","IMPRINT",EDGE,{"disambiguationData":[TD([[subQ11,-1.0]])],"derivedFrom":subQ10}),1.0]])]});}
            var Q15;
            {var subQ1=sQuery(id+"F0.wireOp",EDGE,"E8.0");var subQ5=sQuery(id+"F0.wireOp",EDGE,"E0");var subQ6=makeQuery(id+"F0.imprint","INTERSECT",VERTEX,{"disambiguationData":[OD(0.0)],"derivedFrom":[subQ5,subQ1]});Q15=makeQuery(id+"F0.imprint","IMPRINT",FACE,{"disambiguationData":[TD([[makeQuery(id+"F0.imprint","IMPRINT",EDGE,{"disambiguationData":[TD([[subQ6,1.0]])],"derivedFrom":subQ5}),-1.0]])]});}
            var Q16;
            {var subQ0=sQuery(id+"F0.wireOp",EDGE,"E15.0");var subQ1=sQuery(id+"F0.wireOp",EDGE,"E8.0");var subQ2=makeQuery(id+"F0.imprint","INTERSECT",VERTEX,{"derivedFrom":[subQ1,subQ0]});Q16=makeQuery(id+"F0.imprint","IMPRINT",FACE,{"disambiguationData":[TD([[makeQuery(id+"F0.imprint","IMPRINT",EDGE,{"disambiguationData":[TD([[subQ2,-1.0]])],"derivedFrom":subQ1}),1.0]])]});}
            var Q17;
            {var subQ0=sQuery(id+"F0.wireOp",EDGE,"E14.0");var subQ1=sQuery(id+"F0.wireOp",EDGE,"E8.0");var subQ2=makeQuery(id+"F0.imprint","INTERSECT",VERTEX,{"derivedFrom":[subQ1,subQ0]});Q17=makeQuery(id+"F0.imprint","IMPRINT",FACE,{"disambiguationData":[TD([[makeQuery(id+"F0.imprint","IMPRINT",EDGE,{"disambiguationData":[TD([[subQ2,-1.0]])],"derivedFrom":subQ1}),1.0]])]});}
            var Q18;
            {var subQ7=sQuery(id+"F0.wireOp",EDGE,"E15.0");var subQ9=sQuery(id+"F0.wireOp",EDGE,"E3.top");var subQ11=makeQuery(id+"F0.imprint","INTERSECT",VERTEX,{"derivedFrom":[subQ9,subQ7]});Q18=makeQuery(id+"F0.imprint","IMPRINT",FACE,{"disambiguationData":[TD([[makeQuery(id+"F0.imprint","IMPRINT",EDGE,{"disambiguationData":[TD([[subQ11,-1.0]])],"derivedFrom":subQ9}),-1.0]])]});}
            var Q19;
            {var subQ0=sQuery(id+"F0.wireOp",EDGE,"E6.0");var subQ1=sQuery(id+"F0.wireOp",EDGE,"E0");var subQ2=makeQuery(id+"F0.imprint","INTERSECT",VERTEX,{"disambiguationData":[OD(0.0)],"derivedFrom":[subQ1,subQ0]});Q19=makeQuery(id+"F0.imprint","IMPRINT",FACE,{"disambiguationData":[TD([[makeQuery(id+"F0.imprint","IMPRINT",EDGE,{"disambiguationData":[TD([[subQ2,-1.0]])],"derivedFrom":subQ1}),-1.0]])]});}
            var Q20;
            {var subQ0=sQuery(id+"F0.wireOp",EDGE,"E14.0");var subQ1=sQuery(id+"F0.wireOp",EDGE,"E7.0");var subQ2=makeQuery(id+"F0.imprint","INTERSECT",VERTEX,{"derivedFrom":[subQ1,subQ0]});Q20=makeQuery(id+"F0.imprint","IMPRINT",FACE,{"disambiguationData":[TD([[makeQuery(id+"F0.imprint","IMPRINT",EDGE,{"disambiguationData":[TD([[subQ2,-1.0]])],"derivedFrom":subQ1}),-1.0]])]});}
            var Q21;
            {var subQ0=sQuery(id+"F0.wireOp",EDGE,"E9.0");var subQ1=sQuery(id+"F0.wireOp",EDGE,"E0");var subQ2=makeQuery(id+"F0.imprint","INTERSECT",VERTEX,{"disambiguationData":[OD(1.0)],"derivedFrom":[subQ1,subQ0]});Q21=makeQuery(id+"F0.imprint","IMPRINT",FACE,{"disambiguationData":[TD([[makeQuery(id+"F0.imprint","IMPRINT",EDGE,{"disambiguationData":[TD([[subQ2,-1.0]])],"derivedFrom":subQ1}),-1.0]])]});}
            var Q22;
            {var subQ1=sQuery(id+"F0.wireOp",EDGE,"E6.0");var subQ7=sQuery(id+"F0.wireOp",EDGE,"E0");var subQ9=makeQuery(id+"F0.imprint","INTERSECT",VERTEX,{"disambiguationData":[OD(1.0)],"derivedFrom":[subQ7,subQ1]});Q22=makeQuery(id+"F0.imprint","IMPRINT",FACE,{"disambiguationData":[TD([[makeQuery(id+"F0.imprint","IMPRINT",EDGE,{"disambiguationData":[TD([[subQ9,-1.0]])],"derivedFrom":subQ7}),-1.0]])]});}
            var Q23;
            {var subQ1=sQuery(id+"F0.wireOp",EDGE,"E7.0");var subQ7=sQuery(id+"F0.wireOp",EDGE,"E0");var subQ8=makeQuery(id+"F0.imprint","INTERSECT",VERTEX,{"disambiguationData":[OD(0.0)],"derivedFrom":[subQ7,subQ1]});Q23=makeQuery(id+"F0.imprint","IMPRINT",FACE,{"disambiguationData":[TD([[makeQuery(id+"F0.imprint","IMPRINT",EDGE,{"disambiguationData":[TD([[subQ8,-1.0]])],"derivedFrom":subQ7}),-1.0]])]});}
            var Q24;
            {var subQ1=sQuery(id+"F0.wireOp",EDGE,"E3.left");var subQ6=sQuery(id+"F0.wireOp",EDGE,"E3.bottom");var subQ10=makeQuery(id+"F0.imprint","INTERSECT",VERTEX,{"derivedFrom":[subQ6,subQ1]});Q24=makeQuery(id+"F0.imprint","IMPRINT",FACE,{"disambiguationData":[TD([[makeQuery(id+"F0.imprint","IMPRINT",EDGE,{"disambiguationData":[TD([[subQ10,-1.0]])],"derivedFrom":subQ6}),1.0]])]});}
            var Q25;
            {var subQ0=sQuery(id+"F0.wireOp",EDGE,"E9.0");var subQ1=sQuery(id+"F0.wireOp",EDGE,"E0");var subQ2=makeQuery(id+"F0.imprint","INTERSECT",VERTEX,{"disambiguationData":[OD(0.0)],"derivedFrom":[subQ1,subQ0]});Q25=makeQuery(id+"F0.imprint","IMPRINT",FACE,{"disambiguationData":[TD([[makeQuery(id+"F0.imprint","IMPRINT",EDGE,{"disambiguationData":[TD([[subQ2,1.0]])],"derivedFrom":subQ1}),-1.0]])]});}
            var Q26;
            {var subQ7=sQuery(id+"F0.wireOp",EDGE,"E2.right");var subQ8=sQuery(id+"F0.wireOp",EDGE,"E2.bottom");var subQ9=makeQuery(id+"F0.imprint","INTERSECT",VERTEX,{"derivedFrom":[subQ8,subQ7]});Q26=makeQuery(id+"F0.imprint","IMPRINT",FACE,{"disambiguationData":[TD([[makeQuery(id+"F0.imprint","IMPRINT",EDGE,{"disambiguationData":[TD([[subQ9,1.0]])],"derivedFrom":subQ8}),1.0]])]});}
            var Q27;
            {var subQ1=sQuery(id+"F0.wireOp",EDGE,"E3.top");var subQ6=sQuery(id+"F0.wireOp",EDGE,"E3.left");var subQ10=makeQuery(id+"F0.imprint","INTERSECT",VERTEX,{"derivedFrom":[subQ1,subQ6]});Q27=makeQuery(id+"F0.imprint","IMPRINT",FACE,{"disambiguationData":[TD([[makeQuery(id+"F0.imprint","IMPRINT",EDGE,{"disambiguationData":[TD([[subQ10,-1.0]])],"derivedFrom":subQ1}),-1.0]])]});}
            var Q28;
            {var subQ0=sQuery(id+"F0.wireOp",EDGE,"E15.0");var subQ1=sQuery(id+"F0.wireOp",EDGE,"E7.0");var subQ2=makeQuery(id+"F0.imprint","INTERSECT",VERTEX,{"derivedFrom":[subQ1,subQ0]});Q28=makeQuery(id+"F0.imprint","IMPRINT",FACE,{"disambiguationData":[TD([[makeQuery(id+"F0.imprint","IMPRINT",EDGE,{"disambiguationData":[TD([[subQ2,-1.0]])],"derivedFrom":subQ1}),-1.0]])]});}
            var Q29;
            {var subQ0=sQuery(id+"F0.wireOp",EDGE,"E14.0");var subQ1=sQuery(id+"F0.wireOp",EDGE,"E3.bottom");var subQ2=makeQuery(id+"F0.imprint","INTERSECT",VERTEX,{"derivedFrom":[subQ1,subQ0]});Q29=makeQuery(id+"F0.imprint","IMPRINT",FACE,{"disambiguationData":[TD([[makeQuery(id+"F0.imprint","IMPRINT",EDGE,{"disambiguationData":[TD([[subQ2,-1.0]])],"derivedFrom":subQ1}),1.0]])]});}
            var Q30;
            {var subQ0=sQuery(id+"F0.wireOp",EDGE,"E6.0");var subQ1=sQuery(id+"F0.wireOp",EDGE,"E3.right");var subQ2=makeQuery(id+"F0.imprint","INTERSECT",VERTEX,{"derivedFrom":[subQ1,subQ0]});Q30=makeQuery(id+"F0.imprint","IMPRINT",FACE,{"disambiguationData":[TD([[makeQuery(id+"F0.imprint","IMPRINT",EDGE,{"disambiguationData":[TD([[subQ2,-1.0]])],"derivedFrom":subQ1}),1.0]])]});}
            var Q31;
            {var subQ0=sQuery(id+"F0.wireOp",EDGE,"E6.0");var subQ1=sQuery(id+"F0.wireOp",EDGE,"E3.top");var subQ2=makeQuery(id+"F0.imprint","INTERSECT",VERTEX,{"derivedFrom":[subQ1,subQ0]});Q31=makeQuery(id+"F0.imprint","IMPRINT",FACE,{"disambiguationData":[TD([[makeQuery(id+"F0.imprint","IMPRINT",EDGE,{"disambiguationData":[TD([[subQ2,-1.0]])],"derivedFrom":subQ1}),-1.0]])]});}
            var Q32;
            {var subQ0=sQuery(id+"F0.wireOp",EDGE,"E12.0");var subQ1=sQuery(id+"F0.wireOp",EDGE,"E3.left");var subQ2=makeQuery(id+"F0.imprint","INTERSECT",VERTEX,{"derivedFrom":[subQ1,subQ0]});Q32=makeQuery(id+"F0.imprint","IMPRINT",FACE,{"disambiguationData":[TD([[makeQuery(id+"F0.imprint","IMPRINT",EDGE,{"disambiguationData":[TD([[subQ2,-1.0]])],"derivedFrom":subQ1}),-1.0]])]});}
            var Q33;
            {var subQ0=sQuery(id+"F0.wireOp",EDGE,"E12.0");var subQ1=sQuery(id+"F0.wireOp",EDGE,"E3.right");var subQ2=makeQuery(id+"F0.imprint","INTERSECT",VERTEX,{"derivedFrom":[subQ1,subQ0]});Q33=makeQuery(id+"F0.imprint","IMPRINT",FACE,{"disambiguationData":[TD([[makeQuery(id+"F0.imprint","IMPRINT",EDGE,{"disambiguationData":[TD([[subQ2,-1.0]])],"derivedFrom":subQ1}),1.0]])]});}
            var Q34;
            {var subQ0=sQuery(id+"F0.wireOp",EDGE,"E9.0");var subQ1=sQuery(id+"F0.wireOp",EDGE,"E3.left");var subQ2=makeQuery(id+"F0.imprint","INTERSECT",VERTEX,{"derivedFrom":[subQ1,subQ0]});Q34=makeQuery(id+"F0.imprint","IMPRINT",FACE,{"disambiguationData":[TD([[makeQuery(id+"F0.imprint","IMPRINT",EDGE,{"disambiguationData":[TD([[subQ2,-1.0]])],"derivedFrom":subQ1}),-1.0]])]});}
            var Q35;
            {var subQ0=sQuery(id+"F0.wireOp",EDGE,"E14.0");var subQ1=sQuery(id+"F0.wireOp",EDGE,"E3.top");var subQ2=makeQuery(id+"F0.imprint","INTERSECT",VERTEX,{"derivedFrom":[subQ1,subQ0]});Q35=makeQuery(id+"F0.imprint","IMPRINT",FACE,{"disambiguationData":[TD([[makeQuery(id+"F0.imprint","IMPRINT",EDGE,{"disambiguationData":[TD([[subQ2,-1.0]])],"derivedFrom":subQ1}),-1.0]])]});}
            var Q36;
            {var subQ0=sQuery(id+"F0.wireOp",EDGE,"E8.0");var subQ1=sQuery(id+"F0.wireOp",EDGE,"E3.bottom");var subQ2=makeQuery(id+"F0.imprint","INTERSECT",VERTEX,{"derivedFrom":[subQ1,subQ0]});Q36=makeQuery(id+"F0.imprint","IMPRINT",FACE,{"disambiguationData":[TD([[makeQuery(id+"F0.imprint","IMPRINT",EDGE,{"disambiguationData":[TD([[subQ2,-1.0]])],"derivedFrom":subQ1}),1.0]])]});}
            var Q37;
            {var subQ0=sQuery(id+"F0.wireOp",EDGE,"E8.0");var subQ1=sQuery(id+"F0.wireOp",EDGE,"E0");var subQ2=makeQuery(id+"F0.imprint","INTERSECT",VERTEX,{"disambiguationData":[OD(0.0)],"derivedFrom":[subQ1,subQ0]});Q37=makeQuery(id+"F0.imprint","IMPRINT",FACE,{"disambiguationData":[TD([[makeQuery(id+"F0.imprint","IMPRINT",EDGE,{"disambiguationData":[TD([[subQ2,-1.0]])],"derivedFrom":subQ1}),-1.0]])]});}
            var Q38;
            {var subQ4=sQuery(id+"F0.wireOp",EDGE,"E1.right");var subQ5=sQuery(id+"F0.wireOp",EDGE,"E1.top");var subQ6=makeQuery(id+"F0.imprint","INTERSECT",VERTEX,{"derivedFrom":[subQ5,subQ4]});Q38=makeQuery(id+"F0.imprint","IMPRINT",FACE,{"disambiguationData":[TD([[makeQuery(id+"F0.imprint","IMPRINT",EDGE,{"disambiguationData":[TD([[subQ6,1.0]])],"derivedFrom":subQ5}),-1.0]])]});}
            var Q39;
            {var subQ7=sQuery(id+"F0.wireOp",EDGE,"E1.left");var subQ10=sQuery(id+"F0.wireOp",EDGE,"E1.top");var subQ12=makeQuery(id+"F0.imprint","INTERSECT",VERTEX,{"derivedFrom":[subQ10,subQ7]});Q39=makeQuery(id+"F0.imprint","IMPRINT",FACE,{"disambiguationData":[TD([[makeQuery(id+"F0.imprint","IMPRINT",EDGE,{"disambiguationData":[TD([[subQ12,-1.0]])],"derivedFrom":subQ10}),-1.0]])]});}
            extrude(context, id + "F2", {"entities" : qUnion([Q0, Q1, Q2, Q3, Q4, Q5, Q6, Q7, Q8, Q9, Q10, Q11, Q12, Q13, Q14, Q15, Q16, Q17, Q18, Q19, Q20, Q21, Q22, Q23, Q24, Q25, Q26, Q27, Q28, Q29, Q30, Q31, Q32, Q33, Q34, Q35, Q36, Q37, Q38, Q39]), "depth" : 303 * mm, "offsetDistance" : 25 * mm});
        }
        {
            var Q0;
            {var subQ0=sQuery(id+"F0.wireOp",EDGE,"E12.0");var subQ1=sQuery(id+"F0.wireOp",EDGE,"E6.0");var subQ2=makeQuery(id+"F0.imprint","INTERSECT",VERTEX,{"derivedFrom":[subQ1,subQ0]});Q0=makeQuery(id+"F0.imprint","IMPRINT",FACE,{"disambiguationData":[TD([[makeQuery(id+"F0.imprint","IMPRINT",EDGE,{"disambiguationData":[TD([[subQ2,-1.0]])],"derivedFrom":subQ1}),1.0]])]});}
            var Q1;
            {var subQ5=sQuery(id+"F0.wireOp",EDGE,"E0");var subQ7=sQuery(id+"F0.wireOp",EDGE,"E8.0");var subQ8=makeQuery(id+"F0.imprint","INTERSECT",VERTEX,{"disambiguationData":[OD(1.0)],"derivedFrom":[subQ5,subQ7]});Q1=makeQuery(id+"F0.imprint","IMPRINT",FACE,{"disambiguationData":[TD([[makeQuery(id+"F0.imprint","IMPRINT",EDGE,{"disambiguationData":[TD([[subQ8,-1.0]])],"derivedFrom":subQ5}),-1.0]])]});}
            var Q2;
            {var subQ0=sQuery(id+"F0.wireOp",EDGE,"E6.0");var subQ1=sQuery(id+"F0.wireOp",EDGE,"E3.top");var subQ2=makeQuery(id+"F0.imprint","INTERSECT",VERTEX,{"derivedFrom":[subQ1,subQ0]});Q2=makeQuery(id+"F0.imprint","IMPRINT",FACE,{"disambiguationData":[TD([[makeQuery(id+"F0.imprint","IMPRINT",EDGE,{"disambiguationData":[TD([[subQ2,-1.0]])],"derivedFrom":subQ1}),-1.0]])]});}
            var Q3;
            {var subQ0=sQuery(id+"F0.wireOp",EDGE,"E12.0");var subQ1=sQuery(id+"F0.wireOp",EDGE,"E9.0");var subQ2=makeQuery(id+"F0.imprint","INTERSECT",VERTEX,{"derivedFrom":[subQ1,subQ0]});Q3=makeQuery(id+"F0.imprint","IMPRINT",FACE,{"disambiguationData":[TD([[makeQuery(id+"F0.imprint","IMPRINT",EDGE,{"disambiguationData":[TD([[subQ2,-1.0]])],"derivedFrom":subQ1}),-1.0]])]});}
            var Q4;
            {var subQ7=sQuery(id+"F0.wireOp",EDGE,"E1.left");var subQ10=sQuery(id+"F0.wireOp",EDGE,"E1.top");var subQ12=makeQuery(id+"F0.imprint","INTERSECT",VERTEX,{"derivedFrom":[subQ10,subQ7]});Q4=makeQuery(id+"F0.imprint","IMPRINT",FACE,{"disambiguationData":[TD([[makeQuery(id+"F0.imprint","IMPRINT",EDGE,{"disambiguationData":[TD([[subQ12,-1.0]])],"derivedFrom":subQ10}),-1.0]])]});}
            var Q5;
            {var subQ0=sQuery(id+"F0.wireOp",EDGE,"E13.0");var subQ1=sQuery(id+"F0.wireOp",EDGE,"E9.0");var subQ2=makeQuery(id+"F0.imprint","INTERSECT",VERTEX,{"derivedFrom":[subQ1,subQ0]});Q5=makeQuery(id+"F0.imprint","IMPRINT",FACE,{"disambiguationData":[TD([[makeQuery(id+"F0.imprint","IMPRINT",EDGE,{"disambiguationData":[TD([[subQ2,-1.0]])],"derivedFrom":subQ1}),-1.0]])]});}
            var Q6;
            {var subQ0=sQuery(id+"F0.wireOp",EDGE,"E12.0");var subQ1=sQuery(id+"F0.wireOp",EDGE,"E3.left");var subQ2=makeQuery(id+"F0.imprint","INTERSECT",VERTEX,{"derivedFrom":[subQ1,subQ0]});Q6=makeQuery(id+"F0.imprint","IMPRINT",FACE,{"disambiguationData":[TD([[makeQuery(id+"F0.imprint","IMPRINT",EDGE,{"disambiguationData":[TD([[subQ2,-1.0]])],"derivedFrom":subQ1}),-1.0]])]});}
            var Q7;
            {var subQ1=sQuery(id+"F0.wireOp",EDGE,"E3.right");var subQ5=sQuery(id+"F0.wireOp",EDGE,"E13.0");var subQ10=makeQuery(id+"F0.imprint","INTERSECT",VERTEX,{"derivedFrom":[subQ1,subQ5]});Q7=makeQuery(id+"F0.imprint","IMPRINT",FACE,{"disambiguationData":[TD([[makeQuery(id+"F0.imprint","IMPRINT",EDGE,{"disambiguationData":[TD([[subQ10,-1.0]])],"derivedFrom":subQ1}),1.0]])]});}
            var Q8;
            {var subQ0=sQuery(id+"F0.wireOp",EDGE,"E13.0");var subQ9=sQuery(id+"F0.wireOp",EDGE,"E3.left");var subQ11=makeQuery(id+"F0.imprint","INTERSECT",VERTEX,{"derivedFrom":[subQ9,subQ0]});Q8=makeQuery(id+"F0.imprint","IMPRINT",FACE,{"disambiguationData":[TD([[makeQuery(id+"F0.imprint","IMPRINT",EDGE,{"disambiguationData":[TD([[subQ11,-1.0]])],"derivedFrom":subQ9}),-1.0]])]});}
            var Q9;
            {var subQ1=sQuery(id+"F0.wireOp",EDGE,"E3.bottom");var subQ6=sQuery(id+"F0.wireOp",EDGE,"E3.right");var subQ10=makeQuery(id+"F0.imprint","INTERSECT",VERTEX,{"derivedFrom":[subQ1,subQ6]});Q9=makeQuery(id+"F0.imprint","IMPRINT",FACE,{"disambiguationData":[TD([[makeQuery(id+"F0.imprint","IMPRINT",EDGE,{"disambiguationData":[TD([[subQ10,1.0]])],"derivedFrom":subQ1}),1.0]])]});}
            var Q10;
            {var subQ0=sQuery(id+"F0.wireOp",EDGE,"E13.0");var subQ1=sQuery(id+"F0.wireOp",EDGE,"E6.0");var subQ2=makeQuery(id+"F0.imprint","INTERSECT",VERTEX,{"derivedFrom":[subQ1,subQ0]});Q10=makeQuery(id+"F0.imprint","IMPRINT",FACE,{"disambiguationData":[TD([[makeQuery(id+"F0.imprint","IMPRINT",EDGE,{"disambiguationData":[TD([[subQ2,-1.0]])],"derivedFrom":subQ1}),1.0]])]});}
            var Q11;
            {var subQ0=sQuery(id+"F0.wireOp",EDGE,"E14.0");var subQ1=sQuery(id+"F0.wireOp",EDGE,"E3.top");var subQ2=makeQuery(id+"F0.imprint","INTERSECT",VERTEX,{"derivedFrom":[subQ1,subQ0]});Q11=makeQuery(id+"F0.imprint","IMPRINT",FACE,{"disambiguationData":[TD([[makeQuery(id+"F0.imprint","IMPRINT",EDGE,{"disambiguationData":[TD([[subQ2,-1.0]])],"derivedFrom":subQ1}),-1.0]])]});}
            var Q12;
            {var subQ5=sQuery(id+"F0.wireOp",EDGE,"E2.right");var subQ8=sQuery(id+"F0.wireOp",EDGE,"E2.top");var subQ11=makeQuery(id+"F0.imprint","INTERSECT",VERTEX,{"derivedFrom":[subQ8,subQ5]});Q12=makeQuery(id+"F0.imprint","IMPRINT",FACE,{"disambiguationData":[TD([[makeQuery(id+"F0.imprint","IMPRINT",EDGE,{"disambiguationData":[TD([[subQ11,1.0]])],"derivedFrom":subQ8}),-1.0]])]});}
            var Q13;
            {var subQ5=sQuery(id+"F0.wireOp",EDGE,"E15.0");var subQ9=sQuery(id+"F0.wireOp",EDGE,"E3.bottom");var subQ11=makeQuery(id+"F0.imprint","INTERSECT",VERTEX,{"derivedFrom":[subQ9,subQ5]});Q13=makeQuery(id+"F0.imprint","IMPRINT",FACE,{"disambiguationData":[TD([[makeQuery(id+"F0.imprint","IMPRINT",EDGE,{"disambiguationData":[TD([[subQ11,-1.0]])],"derivedFrom":subQ9}),1.0]])]});}
            var Q14;
            {var subQ7=sQuery(id+"F0.wireOp",EDGE,"E1.right");var subQ8=sQuery(id+"F0.wireOp",EDGE,"E1.bottom");var subQ9=makeQuery(id+"F0.imprint","INTERSECT",VERTEX,{"derivedFrom":[subQ8,subQ7]});Q14=makeQuery(id+"F0.imprint","IMPRINT",FACE,{"disambiguationData":[TD([[makeQuery(id+"F0.imprint","IMPRINT",EDGE,{"disambiguationData":[TD([[subQ9,1.0]])],"derivedFrom":subQ8}),1.0]])]});}
            var Q15;
            {var subQ1=sQuery(id+"F0.wireOp",EDGE,"E3.top");var subQ6=sQuery(id+"F0.wireOp",EDGE,"E3.right");var subQ10=makeQuery(id+"F0.imprint","INTERSECT",VERTEX,{"derivedFrom":[subQ1,subQ6]});Q15=makeQuery(id+"F0.imprint","IMPRINT",FACE,{"disambiguationData":[TD([[makeQuery(id+"F0.imprint","IMPRINT",EDGE,{"disambiguationData":[TD([[subQ10,1.0]])],"derivedFrom":subQ1}),-1.0]])]});}
            var Q16;
            {var subQ0=sQuery(id+"F0.wireOp",EDGE,"E8.0");var subQ1=sQuery(id+"F0.wireOp",EDGE,"E0");var subQ2=makeQuery(id+"F0.imprint","INTERSECT",VERTEX,{"disambiguationData":[OD(0.0)],"derivedFrom":[subQ1,subQ0]});Q16=makeQuery(id+"F0.imprint","IMPRINT",FACE,{"disambiguationData":[TD([[makeQuery(id+"F0.imprint","IMPRINT",EDGE,{"disambiguationData":[TD([[subQ2,-1.0]])],"derivedFrom":subQ1}),-1.0]])]});}
            var Q17;
            {var subQ7=sQuery(id+"F0.wireOp",EDGE,"E2.left");var subQ8=sQuery(id+"F0.wireOp",EDGE,"E2.bottom");var subQ9=makeQuery(id+"F0.imprint","INTERSECT",VERTEX,{"derivedFrom":[subQ8,subQ7]});Q17=makeQuery(id+"F0.imprint","IMPRINT",FACE,{"disambiguationData":[TD([[makeQuery(id+"F0.imprint","IMPRINT",EDGE,{"disambiguationData":[TD([[subQ9,-1.0]])],"derivedFrom":subQ8}),1.0]])]});}
            var Q18;
            {var subQ5=sQuery(id+"F0.wireOp",EDGE,"E2.left");var subQ6=sQuery(id+"F0.wireOp",EDGE,"E2.top");var subQ7=makeQuery(id+"F0.imprint","INTERSECT",VERTEX,{"derivedFrom":[subQ6,subQ5]});Q18=makeQuery(id+"F0.imprint","IMPRINT",FACE,{"disambiguationData":[TD([[makeQuery(id+"F0.imprint","IMPRINT",EDGE,{"disambiguationData":[TD([[subQ7,-1.0]])],"derivedFrom":subQ6}),-1.0]])]});}
            var Q19;
            {var subQ9=sQuery(id+"F0.wireOp",EDGE,"E1.left");var subQ10=sQuery(id+"F0.wireOp",EDGE,"E1.bottom");var subQ11=makeQuery(id+"F0.imprint","INTERSECT",VERTEX,{"derivedFrom":[subQ10,subQ9]});Q19=makeQuery(id+"F0.imprint","IMPRINT",FACE,{"disambiguationData":[TD([[makeQuery(id+"F0.imprint","IMPRINT",EDGE,{"disambiguationData":[TD([[subQ11,-1.0]])],"derivedFrom":subQ10}),1.0]])]});}
            var Q20;
            {var subQ1=sQuery(id+"F0.wireOp",EDGE,"E8.0");var subQ5=sQuery(id+"F0.wireOp",EDGE,"E0");var subQ6=makeQuery(id+"F0.imprint","INTERSECT",VERTEX,{"disambiguationData":[OD(0.0)],"derivedFrom":[subQ5,subQ1]});Q20=makeQuery(id+"F0.imprint","IMPRINT",FACE,{"disambiguationData":[TD([[makeQuery(id+"F0.imprint","IMPRINT",EDGE,{"disambiguationData":[TD([[subQ6,1.0]])],"derivedFrom":subQ5}),-1.0]])]});}
            var Q21;
            {var subQ0=sQuery(id+"F0.wireOp",EDGE,"E15.0");var subQ1=sQuery(id+"F0.wireOp",EDGE,"E8.0");var subQ2=makeQuery(id+"F0.imprint","INTERSECT",VERTEX,{"derivedFrom":[subQ1,subQ0]});Q21=makeQuery(id+"F0.imprint","IMPRINT",FACE,{"disambiguationData":[TD([[makeQuery(id+"F0.imprint","IMPRINT",EDGE,{"disambiguationData":[TD([[subQ2,-1.0]])],"derivedFrom":subQ1}),1.0]])]});}
            var Q22;
            {var subQ0=sQuery(id+"F0.wireOp",EDGE,"E14.0");var subQ1=sQuery(id+"F0.wireOp",EDGE,"E8.0");var subQ2=makeQuery(id+"F0.imprint","INTERSECT",VERTEX,{"derivedFrom":[subQ1,subQ0]});Q22=makeQuery(id+"F0.imprint","IMPRINT",FACE,{"disambiguationData":[TD([[makeQuery(id+"F0.imprint","IMPRINT",EDGE,{"disambiguationData":[TD([[subQ2,-1.0]])],"derivedFrom":subQ1}),1.0]])]});}
            var Q23;
            {var subQ7=sQuery(id+"F0.wireOp",EDGE,"E15.0");var subQ9=sQuery(id+"F0.wireOp",EDGE,"E3.top");var subQ11=makeQuery(id+"F0.imprint","INTERSECT",VERTEX,{"derivedFrom":[subQ9,subQ7]});Q23=makeQuery(id+"F0.imprint","IMPRINT",FACE,{"disambiguationData":[TD([[makeQuery(id+"F0.imprint","IMPRINT",EDGE,{"disambiguationData":[TD([[subQ11,-1.0]])],"derivedFrom":subQ9}),-1.0]])]});}
            var Q24;
            {var subQ0=sQuery(id+"F0.wireOp",EDGE,"E6.0");var subQ1=sQuery(id+"F0.wireOp",EDGE,"E0");var subQ2=makeQuery(id+"F0.imprint","INTERSECT",VERTEX,{"disambiguationData":[OD(0.0)],"derivedFrom":[subQ1,subQ0]});Q24=makeQuery(id+"F0.imprint","IMPRINT",FACE,{"disambiguationData":[TD([[makeQuery(id+"F0.imprint","IMPRINT",EDGE,{"disambiguationData":[TD([[subQ2,-1.0]])],"derivedFrom":subQ1}),-1.0]])]});}
            var Q25;
            {var subQ4=sQuery(id+"F0.wireOp",EDGE,"E1.right");var subQ5=sQuery(id+"F0.wireOp",EDGE,"E1.top");var subQ6=makeQuery(id+"F0.imprint","INTERSECT",VERTEX,{"derivedFrom":[subQ5,subQ4]});Q25=makeQuery(id+"F0.imprint","IMPRINT",FACE,{"disambiguationData":[TD([[makeQuery(id+"F0.imprint","IMPRINT",EDGE,{"disambiguationData":[TD([[subQ6,1.0]])],"derivedFrom":subQ5}),-1.0]])]});}
            var Q26;
            {var subQ0=sQuery(id+"F0.wireOp",EDGE,"E14.0");var subQ1=sQuery(id+"F0.wireOp",EDGE,"E7.0");var subQ2=makeQuery(id+"F0.imprint","INTERSECT",VERTEX,{"derivedFrom":[subQ1,subQ0]});Q26=makeQuery(id+"F0.imprint","IMPRINT",FACE,{"disambiguationData":[TD([[makeQuery(id+"F0.imprint","IMPRINT",EDGE,{"disambiguationData":[TD([[subQ2,-1.0]])],"derivedFrom":subQ1}),-1.0]])]});}
            var Q27;
            {var subQ0=sQuery(id+"F0.wireOp",EDGE,"E9.0");var subQ1=sQuery(id+"F0.wireOp",EDGE,"E0");var subQ2=makeQuery(id+"F0.imprint","INTERSECT",VERTEX,{"disambiguationData":[OD(1.0)],"derivedFrom":[subQ1,subQ0]});Q27=makeQuery(id+"F0.imprint","IMPRINT",FACE,{"disambiguationData":[TD([[makeQuery(id+"F0.imprint","IMPRINT",EDGE,{"disambiguationData":[TD([[subQ2,-1.0]])],"derivedFrom":subQ1}),-1.0]])]});}
            var Q28;
            {var subQ1=sQuery(id+"F0.wireOp",EDGE,"E6.0");var subQ7=sQuery(id+"F0.wireOp",EDGE,"E0");var subQ9=makeQuery(id+"F0.imprint","INTERSECT",VERTEX,{"disambiguationData":[OD(1.0)],"derivedFrom":[subQ7,subQ1]});Q28=makeQuery(id+"F0.imprint","IMPRINT",FACE,{"disambiguationData":[TD([[makeQuery(id+"F0.imprint","IMPRINT",EDGE,{"disambiguationData":[TD([[subQ9,-1.0]])],"derivedFrom":subQ7}),-1.0]])]});}
            var Q29;
            {var subQ1=sQuery(id+"F0.wireOp",EDGE,"E7.0");var subQ7=sQuery(id+"F0.wireOp",EDGE,"E0");var subQ8=makeQuery(id+"F0.imprint","INTERSECT",VERTEX,{"disambiguationData":[OD(0.0)],"derivedFrom":[subQ7,subQ1]});Q29=makeQuery(id+"F0.imprint","IMPRINT",FACE,{"disambiguationData":[TD([[makeQuery(id+"F0.imprint","IMPRINT",EDGE,{"disambiguationData":[TD([[subQ8,-1.0]])],"derivedFrom":subQ7}),-1.0]])]});}
            var Q30;
            {var subQ1=sQuery(id+"F0.wireOp",EDGE,"E3.left");var subQ6=sQuery(id+"F0.wireOp",EDGE,"E3.bottom");var subQ10=makeQuery(id+"F0.imprint","INTERSECT",VERTEX,{"derivedFrom":[subQ6,subQ1]});Q30=makeQuery(id+"F0.imprint","IMPRINT",FACE,{"disambiguationData":[TD([[makeQuery(id+"F0.imprint","IMPRINT",EDGE,{"disambiguationData":[TD([[subQ10,-1.0]])],"derivedFrom":subQ6}),1.0]])]});}
            var Q31;
            {var subQ0=sQuery(id+"F0.wireOp",EDGE,"E9.0");var subQ1=sQuery(id+"F0.wireOp",EDGE,"E0");var subQ2=makeQuery(id+"F0.imprint","INTERSECT",VERTEX,{"disambiguationData":[OD(0.0)],"derivedFrom":[subQ1,subQ0]});Q31=makeQuery(id+"F0.imprint","IMPRINT",FACE,{"disambiguationData":[TD([[makeQuery(id+"F0.imprint","IMPRINT",EDGE,{"disambiguationData":[TD([[subQ2,1.0]])],"derivedFrom":subQ1}),-1.0]])]});}
            var Q32;
            {var subQ7=sQuery(id+"F0.wireOp",EDGE,"E2.right");var subQ8=sQuery(id+"F0.wireOp",EDGE,"E2.bottom");var subQ9=makeQuery(id+"F0.imprint","INTERSECT",VERTEX,{"derivedFrom":[subQ8,subQ7]});Q32=makeQuery(id+"F0.imprint","IMPRINT",FACE,{"disambiguationData":[TD([[makeQuery(id+"F0.imprint","IMPRINT",EDGE,{"disambiguationData":[TD([[subQ9,1.0]])],"derivedFrom":subQ8}),1.0]])]});}
            var Q33;
            {var subQ1=sQuery(id+"F0.wireOp",EDGE,"E3.top");var subQ6=sQuery(id+"F0.wireOp",EDGE,"E3.left");var subQ10=makeQuery(id+"F0.imprint","INTERSECT",VERTEX,{"derivedFrom":[subQ1,subQ6]});Q33=makeQuery(id+"F0.imprint","IMPRINT",FACE,{"disambiguationData":[TD([[makeQuery(id+"F0.imprint","IMPRINT",EDGE,{"disambiguationData":[TD([[subQ10,-1.0]])],"derivedFrom":subQ1}),-1.0]])]});}
            var Q34;
            {var subQ0=sQuery(id+"F0.wireOp",EDGE,"E15.0");var subQ1=sQuery(id+"F0.wireOp",EDGE,"E7.0");var subQ2=makeQuery(id+"F0.imprint","INTERSECT",VERTEX,{"derivedFrom":[subQ1,subQ0]});Q34=makeQuery(id+"F0.imprint","IMPRINT",FACE,{"disambiguationData":[TD([[makeQuery(id+"F0.imprint","IMPRINT",EDGE,{"disambiguationData":[TD([[subQ2,-1.0]])],"derivedFrom":subQ1}),-1.0]])]});}
            var Q35;
            {var subQ0=sQuery(id+"F0.wireOp",EDGE,"E14.0");var subQ1=sQuery(id+"F0.wireOp",EDGE,"E3.bottom");var subQ2=makeQuery(id+"F0.imprint","INTERSECT",VERTEX,{"derivedFrom":[subQ1,subQ0]});Q35=makeQuery(id+"F0.imprint","IMPRINT",FACE,{"disambiguationData":[TD([[makeQuery(id+"F0.imprint","IMPRINT",EDGE,{"disambiguationData":[TD([[subQ2,-1.0]])],"derivedFrom":subQ1}),1.0]])]});}
            var Q36;
            {var subQ0=sQuery(id+"F0.wireOp",EDGE,"E6.0");var subQ1=sQuery(id+"F0.wireOp",EDGE,"E3.right");var subQ2=makeQuery(id+"F0.imprint","INTERSECT",VERTEX,{"derivedFrom":[subQ1,subQ0]});Q36=makeQuery(id+"F0.imprint","IMPRINT",FACE,{"disambiguationData":[TD([[makeQuery(id+"F0.imprint","IMPRINT",EDGE,{"disambiguationData":[TD([[subQ2,-1.0]])],"derivedFrom":subQ1}),1.0]])]});}
            var Q37;
            {var subQ0=sQuery(id+"F0.wireOp",EDGE,"E12.0");var subQ1=sQuery(id+"F0.wireOp",EDGE,"E3.right");var subQ2=makeQuery(id+"F0.imprint","INTERSECT",VERTEX,{"derivedFrom":[subQ1,subQ0]});Q37=makeQuery(id+"F0.imprint","IMPRINT",FACE,{"disambiguationData":[TD([[makeQuery(id+"F0.imprint","IMPRINT",EDGE,{"disambiguationData":[TD([[subQ2,-1.0]])],"derivedFrom":subQ1}),1.0]])]});}
            var Q38;
            {var subQ0=sQuery(id+"F0.wireOp",EDGE,"E9.0");var subQ1=sQuery(id+"F0.wireOp",EDGE,"E3.left");var subQ2=makeQuery(id+"F0.imprint","INTERSECT",VERTEX,{"derivedFrom":[subQ1,subQ0]});Q38=makeQuery(id+"F0.imprint","IMPRINT",FACE,{"disambiguationData":[TD([[makeQuery(id+"F0.imprint","IMPRINT",EDGE,{"disambiguationData":[TD([[subQ2,-1.0]])],"derivedFrom":subQ1}),-1.0]])]});}
            var Q39;
            {var subQ0=sQuery(id+"F0.wireOp",EDGE,"E8.0");var subQ1=sQuery(id+"F0.wireOp",EDGE,"E3.bottom");var subQ2=makeQuery(id+"F0.imprint","INTERSECT",VERTEX,{"derivedFrom":[subQ1,subQ0]});Q39=makeQuery(id+"F0.imprint","IMPRINT",FACE,{"disambiguationData":[TD([[makeQuery(id+"F0.imprint","IMPRINT",EDGE,{"disambiguationData":[TD([[subQ2,-1.0]])],"derivedFrom":subQ1}),1.0]])]});}
            extrude(context, id + "F3", {"entities" : qUnion([Q0, Q1, Q2, Q3, Q4, Q5, Q6, Q7, Q8, Q9, Q10, Q11, Q12, Q13, Q14, Q15, Q16, Q17, Q18, Q19, Q20, Q21, Q22, Q23, Q24, Q25, Q26, Q27, Q28, Q29, Q30, Q31, Q32, Q33, Q34, Q35, Q36, Q37, Q38, Q39]), "depth" : 350 * mm, "offsetDistance" : 25 * mm});
        }
    });
